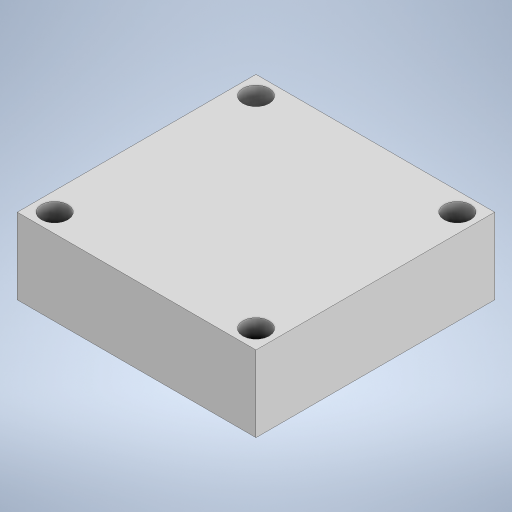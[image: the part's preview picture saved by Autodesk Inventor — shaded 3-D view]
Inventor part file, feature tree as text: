
AUTODESK INVENTOR PART (.ipt)
format: ipt  version: 2023 (Build 270158000, 158)  size: 207,360 bytes
history: native  units: in
note: dims shown in document units (in); Inventor stores cm internally (conversion verified against a paired STEP export)
features: extrude x2, sketch x2, projected_geometry x1
ambient origin geometry x8: Origin, YZ Plane, XZ Plane, XY Plane, X Axis, Y Axis, Z Axis, Center Point
bodies: Solid1 (feature_tree)
feature tree (5):
  extrude  "Extrusion1"  Depth=1.4232in
  extrude  "Extrusion2"  Depth=0.4528in
  sketch  "Sketch1"  dims[d0=1.4232in d1=1.4232in]
  sketch  "Sketch2"  dims[d2=0.4528in d3=0.0in d4=0.6004in d5=0.6004in d6=0.1575in d7=1.5748in d9=360.0deg d11=0.4528in d12=0.0in]
  projected_geometry  "Projected Loop1"
